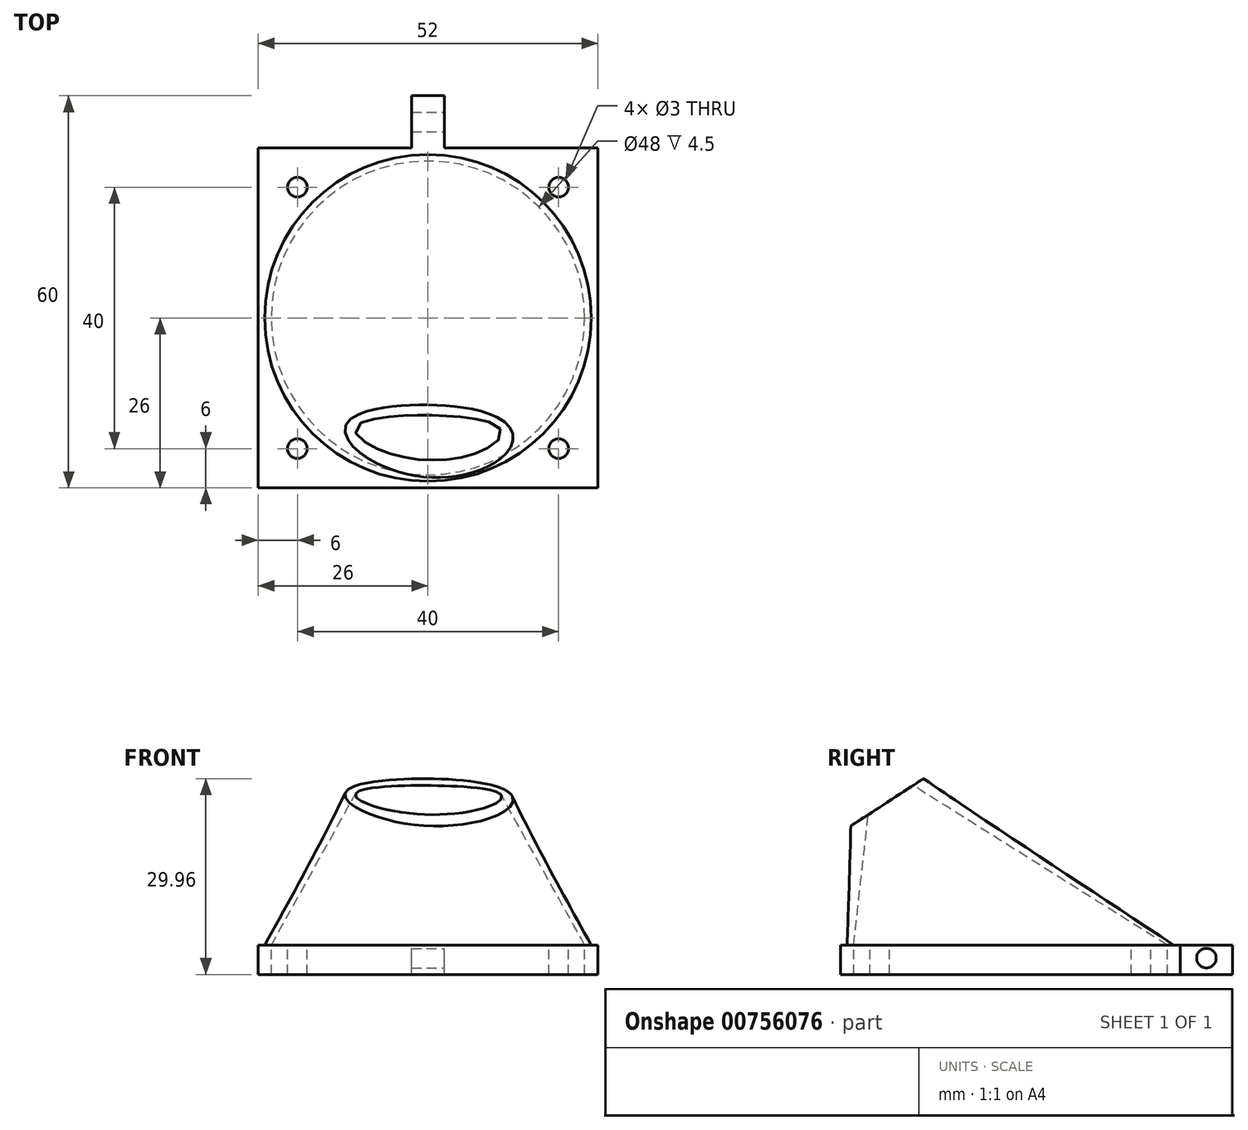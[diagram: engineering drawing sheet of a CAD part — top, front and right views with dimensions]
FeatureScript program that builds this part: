
annotation { "Feature Type Name" : "Feature", "Feature Type Description" : "" }
export const myFeature = defineFeature(function(context is Context, id is Id, definition is map)
    precondition{}
    {
        {
            var Q0;
            Q0=qCreatedBy(makeId("Top.planeOp"),FACE);
            var sketch = newSketch(context, id + "F0", { "sketchPlane" : qUnion([Q0])});
            skPoint(sketch, "E0.middle", {"position": v(0, 0) * mm});
            skCircle(sketch, "E1", {"center": v(0, 0) * mm, "radius": 24 * mm});
            skLineSegment(sketch, "E2.bottom", {"start": v(26, -26) * mm, "end": v(-26, -26) * mm});
            skLineSegment(sketch, "E2.top", {"start": v(26, 26) * mm, "end": v(-26, 26) * mm});
            skLineSegment(sketch, "E2.left", {"start": v(26, -26) * mm, "end": v(26, 26) * mm});
            skLineSegment(sketch, "E2.right", {"start": v(-26, -26) * mm, "end": v(-26, 26) * mm});
            skCircle(sketch, "E3", {"center": v(20, -20) * mm, "radius": 1.5 * mm});
            skCircle(sketch, "E4.MirrorC", {"center": v(-20, -20) * mm, "radius": 1.5 * mm});
            skCircle(sketch, "E5.MirrorC", {"center": v(20, 20) * mm, "radius": 1.5 * mm});
            skCircle(sketch, "E6.MirrorC", {"center": v(-20, 20) * mm, "radius": 1.5 * mm});
            skLineSegment(sketch, "E7.bottom", {"start": v(2.5, 26) * mm, "end": v(-2.5, 26) * mm});
            skLineSegment(sketch, "E7.top", {"start": v(2.5, 34) * mm, "end": v(-2.5, 34) * mm});
            skLineSegment(sketch, "E7.left", {"start": v(2.5, 26) * mm, "end": v(2.5, 34) * mm});
            skLineSegment(sketch, "E7.right", {"start": v(-2.5, 26) * mm, "end": v(-2.5, 34) * mm});
            skPoint(sketch, "E7.middle", {"position": v(0, 30) * mm});
            skLineSegment(sketch, "E8.0", {"start": v(2.5, 30) * mm, "end": v(-2.5, 30) * mm});
            skLineSegment(sketch, "E9.0", {"start": v(2.5, 31.5) * mm, "end": v(-2.5, 31.5) * mm});
            skLineSegment(sketch, "E10.0", {"start": v(2.5, 28.5) * mm, "end": v(-2.5, 28.5) * mm});
            skSolve(sketch);
        }
        {
            var Q0;
            Q0=qCreatedBy(makeId("Top.planeOp"),FACE);
            cPlane(context, id + "F1", {"entities" : qUnion([Q0]), "cplaneType" : CPlaneType.OFFSET, "offset" : 27 * mm, "width" : 150 * mm, "height" : 150 * mm});
        }
        {
            var Q0;
            Q0=qCreatedBy(id+"F1.planeOp",FACE);
            var sketch = newSketch(context, id + "F2", { "sketchPlane" : qUnion([Q0])});
            skEllipse(sketch, "E11", {"center": v(0, -20) * mm, "majorRadius": 9 * mm, "minorRadius": 1 * mm, "majorAxis": v(1, 0)});
            skSolve(sketch);
        }
        {
            var Q0;
            Q0=makeQuery(id+"F0.imprint","IMPRINT",FACE,{"disambiguationData":[TD([[makeQuery(id+"F0.imprint","IMPRINT",EDGE,{"derivedFrom":sQuery(id+"F0.wireOp",EDGE,"E1")}),1.0]])]});
            var Q1;
            Q1=makeQuery(id+"F2.imprint","IMPRINT",FACE,{"disambiguationData":[TD([[makeQuery(id+"F2.imprint","IMPRINT",EDGE,{"derivedFrom":sQuery(id+"F2.wireOp",EDGE,"E11")}),1.0]])]});
            loft(context, id + "F3", {"sheetProfilesArray" : [{ "sheetProfileEntities" : qUnion([Q0]) }, { "sheetProfileEntities" : qUnion([Q1]) }]});
        }
        {
            var Q0;
            Q0=qCreatedBy(makeId("Top.planeOp"),FACE);
            var sketch = newSketch(context, id + "F4", { "sketchPlane" : qUnion([Q0])});
            skCircle(sketch, "E12", {"center": v(0, 0) * mm, "radius": 25 * mm});
            skSolve(sketch);
        }
        {
            var Q0;
            Q0=qCreatedBy(id+"F1.planeOp",FACE);
            var sketch = newSketch(context, id + "F5", { "sketchPlane" : qUnion([Q0])});
            skEllipse(sketch, "E13", {"center": v(0, -20) * mm, "majorRadius": 11 * mm, "minorRadius": 4.5 * mm, "majorAxis": v(1, 0)});
            skSolve(sketch);
        }
        {
            var Q1;
            Q1=makeQuery(id+"F4.imprint","IMPRINT",FACE,{"disambiguationData":[TD([[makeQuery(id+"F4.imprint","IMPRINT",EDGE,{"derivedFrom":sQuery(id+"F4.wireOp",EDGE,"E12")}),1.0]])]});
            var Q2;
            Q2=makeQuery(id+"F5.imprint","IMPRINT",FACE,{"disambiguationData":[TD([[makeQuery(id+"F5.imprint","IMPRINT",EDGE,{"derivedFrom":sQuery(id+"F5.wireOp",EDGE,"E13")}),1.0]])]});
            loft(context, id + "F6", {"sheetProfilesArray" : [{ "sheetProfileEntities" : qUnion([Q1]) }, { "sheetProfileEntities" : qUnion([Q2]) }]});
        }
        {
            var Q0;
            Q0=makeQuery(id+"F3.opLoft","SWEPT_BODY",BODY,{"disambiguationData":[OSD([makeQuery(id+"F0.imprint","IMPRINT",FACE,{"disambiguationData":[TD([[makeQuery(id+"F0.imprint","IMPRINT",EDGE,{"derivedFrom":sQuery(id+"F0.wireOp",EDGE,"E1")}),1.0]])]}),makeQuery(id+"F2.imprint","IMPRINT",FACE,{"disambiguationData":[TD([[makeQuery(id+"F2.imprint","IMPRINT",EDGE,{"derivedFrom":sQuery(id+"F2.wireOp",EDGE,"E11")}),1.0]])]})])]});
            var Q1;
            Q1=makeQuery(id+"F6.opLoft","SWEPT_BODY",BODY,{"disambiguationData":[OSD([makeQuery(id+"F4.imprint","IMPRINT",FACE,{"disambiguationData":[TD([[makeQuery(id+"F4.imprint","IMPRINT",EDGE,{"derivedFrom":sQuery(id+"F4.wireOp",EDGE,"E12")}),1.0]])]}),makeQuery(id+"F5.imprint","IMPRINT",FACE,{"disambiguationData":[TD([[makeQuery(id+"F5.imprint","IMPRINT",EDGE,{"derivedFrom":sQuery(id+"F5.wireOp",EDGE,"E13")}),1.0]])]})])]});
            booleanBodies(context, id + "F7", {"operationType" : BooleanOperationType.SUBTRACTION, "tools" : qUnion([Q0]), "targets" : qUnion([Q1])});
        }
        {
            var Q0;
            Q0=makeQuery(id+"F0.imprint","IMPRINT",FACE,{"disambiguationData":[TD([[makeQuery(id+"F0.imprint","IMPRINT",EDGE,{"derivedFrom":sQuery(id+"F0.wireOp",EDGE,"E1")}),-1.0]])]});
            var Q1;
            {var subQ5=sQuery(id+"F0.wireOp",EDGE,"E10.0");Q1=makeQuery(id+"F0.imprint","IMPRINT",FACE,{"disambiguationData":[TD([[makeQuery(id+"F0.imprint","IMPRINT",EDGE,{"derivedFrom":subQ5}),1.0]])]});}
            var Q2;
            {var subQ0=sQuery(id+"F0.wireOp",EDGE,"E8.0");Q2=makeQuery(id+"F0.imprint","IMPRINT",FACE,{"disambiguationData":[TD([[makeQuery(id+"F0.imprint","IMPRINT",EDGE,{"derivedFrom":subQ0}),1.0]])]});}
            var Q3;
            {var subQ2=sQuery(id+"F0.wireOp",EDGE,"E8.0");Q3=makeQuery(id+"F0.imprint","IMPRINT",FACE,{"disambiguationData":[TD([[makeQuery(id+"F0.imprint","IMPRINT",EDGE,{"derivedFrom":subQ2}),-1.0]])]});}
            var Q4;
            {var subQ0=sQuery(id+"F0.wireOp",EDGE,"E7.top");Q4=makeQuery(id+"F0.imprint","IMPRINT",FACE,{"disambiguationData":[TD([[makeQuery(id+"F0.imprint","IMPRINT",EDGE,{"derivedFrom":subQ0}),1.0]])]});}
            extrude(context, id + "F8", {"entities" : qUnion([Q0, Q1, Q2, Q3, Q4]), "operationType" : NewBodyOperationType.ADD, "oppositeDirection" : true, "depth" : 4.5 * mm});
        }
        {
            var Q0;
            {var subQ0=sQuery(id+"F0.wireOp",EDGE,"E8.0");Q0=makeQuery(id+"F0.imprint","IMPRINT",FACE,{"disambiguationData":[TD([[makeQuery(id+"F0.imprint","IMPRINT",EDGE,{"derivedFrom":subQ0}),1.0]])]});}
            var Q1;
            Q1=sQuery(id+"F0.wireOp",EDGE,"E8.0");
            revolve(context, id + "F9", {"entities" : qUnion([Q0]), "axis" : qUnion([Q1]), "revolveType" : RevolveType.FULL});
        }
        {
            var Q0;
            Q0=makeQuery(id+"F9.opRevolve","SWEPT_BODY",BODY,{"disambiguationData":[OSD([sQuery(id+"F0.wireOp",EDGE,"E7.left"),sQuery(id+"F0.wireOp",EDGE,"E7.right"),sQuery(id+"F0.wireOp",EDGE,"E8.0"),sQuery(id+"F0.wireOp",EDGE,"E10.0")])]});
            transform(context, id + "F10", {"entities" : qUnion([Q0]), "transformType" : TransformType.TRANSLATION_3D, "dx" : 0 * mm, "dy" : 0 * mm, "dz" : -2 * mm, "makeCopy" : false});
        }
        {
            var Q0;
            Q0=makeQuery(id+"F9.opRevolve","SWEPT_BODY",BODY,{"disambiguationData":[OSD([sQuery(id+"F0.wireOp",EDGE,"E7.left"),sQuery(id+"F0.wireOp",EDGE,"E7.right"),sQuery(id+"F0.wireOp",EDGE,"E8.0"),sQuery(id+"F0.wireOp",EDGE,"E10.0")])]});
            var Q1;
            Q1=makeQuery(id+"F6.opLoft","SWEPT_BODY",BODY,{"disambiguationData":[OSD([makeQuery(id+"F4.imprint","IMPRINT",FACE,{"disambiguationData":[TD([[makeQuery(id+"F4.imprint","IMPRINT",EDGE,{"derivedFrom":sQuery(id+"F4.wireOp",EDGE,"E12")}),1.0]])]}),makeQuery(id+"F5.imprint","IMPRINT",FACE,{"disambiguationData":[TD([[makeQuery(id+"F5.imprint","IMPRINT",EDGE,{"derivedFrom":sQuery(id+"F5.wireOp",EDGE,"E13")}),1.0]])]})])]});
            booleanBodies(context, id + "F11", {"operationType" : BooleanOperationType.SUBTRACTION, "tools" : qUnion([Q0]), "targets" : qUnion([Q1])});
        }
        {
            var Q0;
            Q0=qCreatedBy(makeId("Right.planeOp"),FACE);
            var sketch = newSketch(context, id + "F12", { "sketchPlane" : qUnion([Q0])});
            skLineSegment(sketch, "E14", {"start": v(-34, 12) * mm, "end": v(-9.4, 28) * mm});
            skLineSegment(sketch, "E15", {"start": v(-9.4, 28) * mm, "end": v(-9.4, 38) * mm});
            skLineSegment(sketch, "E16", {"start": v(-9.4, 38) * mm, "end": v(-34, 38) * mm});
            skLineSegment(sketch, "E17", {"start": v(-34, 38) * mm, "end": v(-34, 12) * mm});
            skSolve(sketch);
        }
        {
            var Q0;
            Q0=makeQuery(id+"F12.imprint","IMPRINT",FACE,{"disambiguationData":[TD([[makeQuery(id+"F12.imprint","IMPRINT",EDGE,{"derivedFrom":sQuery(id+"F12.wireOp",EDGE,"E14")}),1.0]])]});
            extrude(context, id + "F13", {"entities" : qUnion([Q0]), "operationType" : NewBodyOperationType.REMOVE, "depth" : 25 * mm, "hasSecondDirection" : true, "secondDirectionOppositeDirection" : true, "secondDirectionDepth" : 25 * mm});
        }
    });
